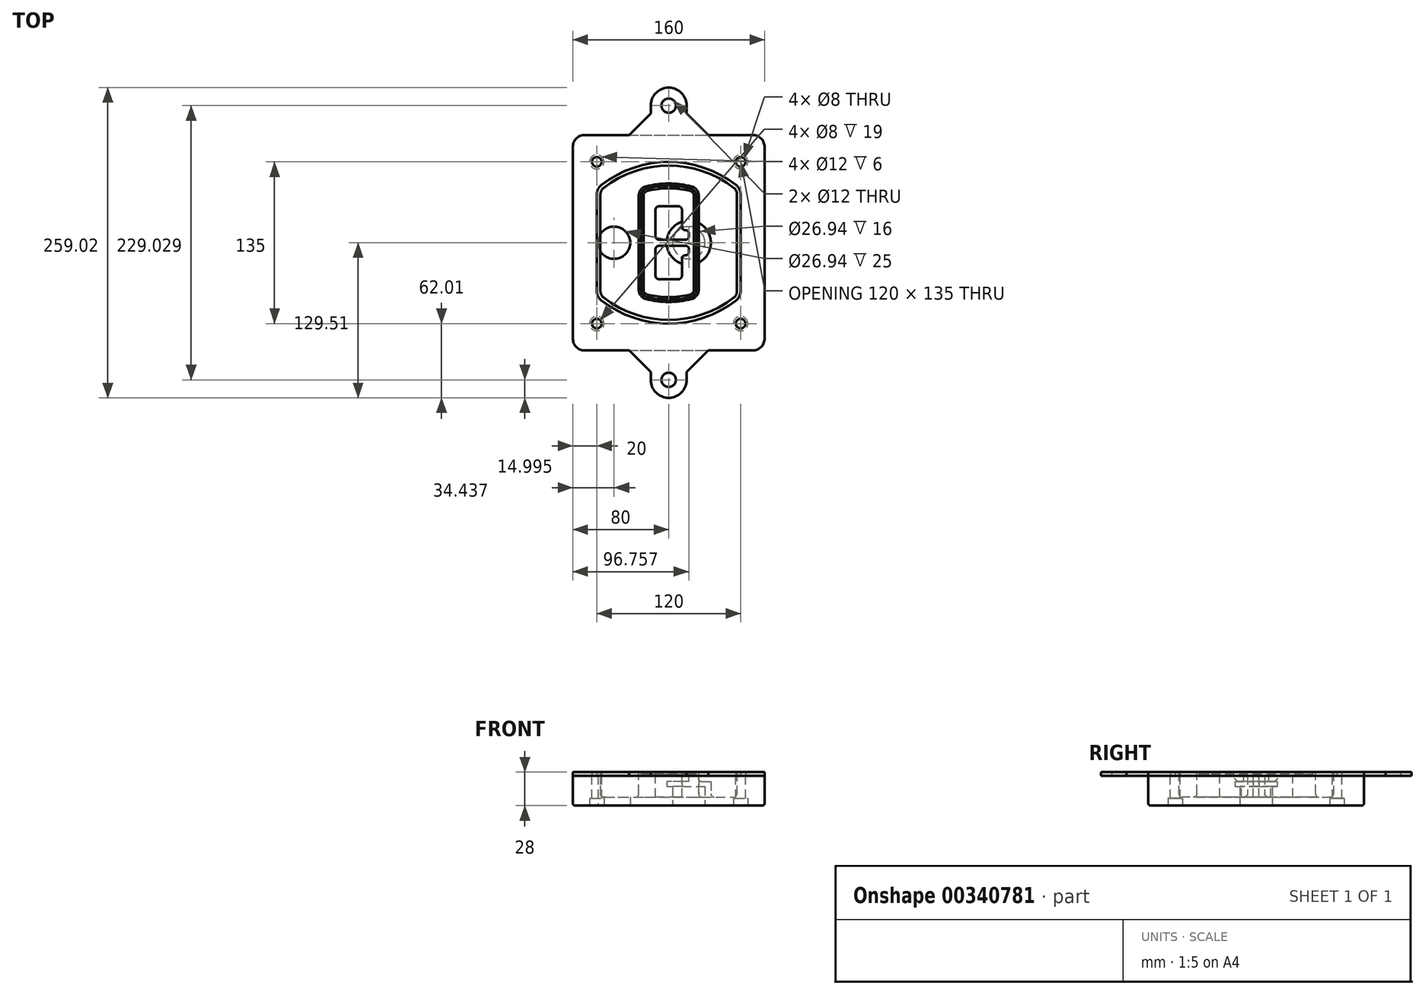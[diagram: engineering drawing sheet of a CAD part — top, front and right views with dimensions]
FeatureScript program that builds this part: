
annotation { "Feature Type Name" : "Feature", "Feature Type Description" : "" }
export const myFeature = defineFeature(function(context is Context, id is Id, definition is map)
    precondition{}
    {
        {
            var Q0;
            Q0=qCreatedBy(makeId("Top.planeOp"),FACE);
            var sketch = newSketch(context, id + "F0", { "sketchPlane" : qUnion([Q0])});
            skPoint(sketch, "E0.rect.middle", {"position": v(0, 0) * mm});
            skLineSegment(sketch, "E1.bottom", {"start": v(-70, -90) * mm, "end": v(70, -90) * mm});
            skLineSegment(sketch, "E1.top", {"start": v(-70, 90) * mm, "end": v(70, 90) * mm});
            skLineSegment(sketch, "E1.left", {"start": v(-80, -80) * mm, "end": v(-80, 80) * mm});
            skLineSegment(sketch, "E1.right", {"start": v(80, -80) * mm, "end": v(80, 80) * mm});
            skLineSegment(sketch, "E2", {"start": v(-80, 90) * mm, "end": v(80, -90) * mm, "construction": true});
            skLineSegment(sketch, "E3", {"start": v(80, 90) * mm, "end": v(-80, -90) * mm, "construction": true});
            skCircle(sketch, "E4", {"center": v(-60, 67.5) * mm, "radius": 4 * mm});
            skCircle(sketch, "E5", {"center": v(60, 67.5) * mm, "radius": 4 * mm});
            skCircle(sketch, "E6", {"center": v(60, -67.5) * mm, "radius": 4 * mm});
            skCircle(sketch, "E7", {"center": v(-60, -67.5) * mm, "radius": 4 * mm});
            skLineSegment(sketch, "E8", {"start": v(-60, 67.5) * mm, "end": v(60, 67.5) * mm, "construction": true});
            skLineSegment(sketch, "E9", {"start": v(60, 67.5) * mm, "end": v(60, -67.5) * mm, "construction": true});
            skLineSegment(sketch, "E10", {"start": v(60, -67.5) * mm, "end": v(-60, -67.5) * mm, "construction": true});
            skLineSegment(sketch, "E11", {"start": v(-60, -67.5) * mm, "end": v(-60, 67.5) * mm, "construction": true});
            skLineSegment(sketch, "E12", {"start": v(-60, 40.3) * mm, "end": v(-60, -40.3) * mm});
            skLineSegment(sketch, "E13", {"start": v(60, 40.3) * mm, "end": v(60, -40.3) * mm});
            skArc(sketch, "E14", {"start": v(56.15, 48.18) * mm, "mid": v(0, 67.5) * mm, "end": v(-56.15, 48.18) * mm});
            skArc(sketch, "E15", {"start": v(-56.15, -48.18) * mm, "mid": v(0, -67.5) * mm, "end": v(56.15, -48.18) * mm});
            skLineSegment(sketch, "E16", {"start": v(-60, 0) * mm, "end": v(60, 0) * mm, "construction": true});
            skPoint(sketch, "E17.visualSharp", {"position": v(-60, -45) * mm});
            skArc(sketch, "E17.filletArc", {"start": v(-60, -40.3) * mm, "mid": v(-58.99, -44.68) * mm, "end": v(-56.15, -48.18) * mm});
            skPoint(sketch, "E18.visualSharp", {"position": v(-60, 45) * mm});
            skArc(sketch, "E18.filletArc", {"start": v(-56.15, 48.18) * mm, "mid": v(-58.99, 44.68) * mm, "end": v(-60, 40.3) * mm});
            skPoint(sketch, "E19.visualSharp", {"position": v(60, 45) * mm});
            skArc(sketch, "E19.filletArc", {"start": v(60, 40.3) * mm, "mid": v(58.99, 44.68) * mm, "end": v(56.15, 48.18) * mm});
            skPoint(sketch, "E20.visualSharp", {"position": v(60, -45) * mm});
            skArc(sketch, "E20.filletArc", {"start": v(56.15, -48.18) * mm, "mid": v(58.99, -44.68) * mm, "end": v(60, -40.3) * mm});
            skPoint(sketch, "E21.visualSharp", {"position": v(-80, 90) * mm});
            skArc(sketch, "E21.filletArc", {"start": v(-70, 90) * mm, "mid": v(-77.07, 87.07) * mm, "end": v(-80, 80) * mm});
            skPoint(sketch, "E22.visualSharp", {"position": v(80, 90) * mm});
            skArc(sketch, "E22.filletArc", {"start": v(80, 80) * mm, "mid": v(77.07, 87.07) * mm, "end": v(70, 90) * mm});
            skPoint(sketch, "E23.visualSharp", {"position": v(80, -90) * mm});
            skArc(sketch, "E23.filletArc", {"start": v(70, -90) * mm, "mid": v(77.07, -87.07) * mm, "end": v(80, -80) * mm});
            skPoint(sketch, "E24.visualSharp", {"position": v(-80, -90) * mm});
            skArc(sketch, "E24.filletArc", {"start": v(-80, -80) * mm, "mid": v(-77.07, -87.07) * mm, "end": v(-70, -90) * mm});
            skArc(sketch, "E25.0", {"start": v(57, 40.3) * mm, "mid": v(56.3, 43.36) * mm, "end": v(54.3, 45.81) * mm});
            skLineSegment(sketch, "E25.1", {"start": v(57, 40.3) * mm, "end": v(57, -40.3) * mm});
            skArc(sketch, "E25.2", {"start": v(54.3, -45.81) * mm, "mid": v(56.3, -43.36) * mm, "end": v(57, -40.3) * mm});
            skArc(sketch, "E25.3", {"start": v(-54.3, -45.81) * mm, "mid": v(0, -64.5) * mm, "end": v(54.3, -45.81) * mm});
            skArc(sketch, "E25.4", {"start": v(-57, -40.3) * mm, "mid": v(-56.3, -43.36) * mm, "end": v(-54.3, -45.81) * mm});
            skArc(sketch, "E25.5", {"start": v(54.3, 45.81) * mm, "mid": v(0, 64.5) * mm, "end": v(-54.3, 45.81) * mm});
            skLineSegment(sketch, "E25.6", {"start": v(-57, 40.3) * mm, "end": v(-57, -40.3) * mm});
            skArc(sketch, "E25.7", {"start": v(-54.3, 45.81) * mm, "mid": v(-56.3, 43.36) * mm, "end": v(-57, 40.3) * mm});
            skArc(sketch, "E26.0", {"start": v(-58.62, 51.33) * mm, "mid": v(-62.58, 46.43) * mm, "end": v(-64, 40.3) * mm});
            skArc(sketch, "E26.1", {"start": v(58.62, 51.33) * mm, "mid": v(0, 71.5) * mm, "end": v(-58.62, 51.33) * mm});
            skArc(sketch, "E26.2", {"start": v(64, 40.3) * mm, "mid": v(62.58, 46.43) * mm, "end": v(58.62, 51.33) * mm});
            skLineSegment(sketch, "E26.3", {"start": v(64, 40.3) * mm, "end": v(64, -40.3) * mm});
            skArc(sketch, "E26.4", {"start": v(58.62, -51.33) * mm, "mid": v(62.58, -46.43) * mm, "end": v(64, -40.3) * mm});
            skLineSegment(sketch, "E26.5", {"start": v(-64, 40.3) * mm, "end": v(-64, -40.3) * mm});
            skArc(sketch, "E26.6", {"start": v(-58.62, -51.33) * mm, "mid": v(0, -71.5) * mm, "end": v(58.62, -51.33) * mm});
            skArc(sketch, "E26.7", {"start": v(-64, -40.3) * mm, "mid": v(-62.58, -46.43) * mm, "end": v(-58.62, -51.33) * mm});
            skSolve(sketch);
        }
        {
            var Q0;
            Q0=makeQuery(id+"F0.imprint","IMPRINT",FACE,{"disambiguationData":[TD([[makeQuery(id+"F0.imprint","IMPRINT",EDGE,{"derivedFrom":sQuery(id+"F0.wireOp",EDGE,"E1.bottom")}),1.0]])]});
            var Q1;
            Q1=makeQuery(id+"F0.imprint","IMPRINT",FACE,{"disambiguationData":[TD([[makeQuery(id+"F0.imprint","IMPRINT",EDGE,{"derivedFrom":sQuery(id+"F0.wireOp",EDGE,"E12")}),1.0]])]});
            var Q2;
            Q2=makeQuery(id+"F0.imprint","IMPRINT",FACE,{"disambiguationData":[TD([[makeQuery(id+"F0.imprint","IMPRINT",EDGE,{"derivedFrom":sQuery(id+"F0.wireOp",EDGE,"E25.0")}),1.0]])]});
            var Q3;
            Q3=makeQuery(id+"F0.imprint","IMPRINT",FACE,{"disambiguationData":[TD([[makeQuery(id+"F0.imprint","IMPRINT",EDGE,{"derivedFrom":sQuery(id+"F0.wireOp",EDGE,"E12")}),-1.0]])]});
            extrude(context, id + "F1", {"entities" : qUnion([Q0, Q1, Q2, Q3]), "oppositeDirection" : true, "depth" : 25 * mm});
        }
        {
            var Q0;
            Q0=makeQuery(id+"F0.imprint","IMPRINT",FACE,{"disambiguationData":[TD([[makeQuery(id+"F0.imprint","IMPRINT",EDGE,{"derivedFrom":sQuery(id+"F0.wireOp",EDGE,"E12")}),1.0]])]});
            extrude(context, id + "F2", {"entities" : qUnion([Q0]), "operationType" : NewBodyOperationType.ADD, "depth" : 3 * mm});
        }
        {
            var Q0;
            Q0=makeQuery(id+"F0.imprint","IMPRINT",FACE,{"disambiguationData":[TD([[makeQuery(id+"F0.imprint","IMPRINT",EDGE,{"derivedFrom":sQuery(id+"F0.wireOp",EDGE,"E25.0")}),1.0]])]});
            extrude(context, id + "F3", {"entities" : qUnion([Q0]), "operationType" : NewBodyOperationType.REMOVE, "oppositeDirection" : true, "depth" : 18 * mm});
        }
        {
            var Q0;
            Q0=makeQuery(id+"F2.opExtrude","CAP_FACE",FACE,{"disambiguationData":[OSD([sQuery(id+"F0.wireOp",EDGE,"E12"),sQuery(id+"F0.wireOp",EDGE,"E13"),sQuery(id+"F0.wireOp",EDGE,"E14"),sQuery(id+"F0.wireOp",EDGE,"E15"),sQuery(id+"F0.wireOp",EDGE,"E17.filletArc"),sQuery(id+"F0.wireOp",EDGE,"E18.filletArc"),sQuery(id+"F0.wireOp",EDGE,"E19.filletArc"),sQuery(id+"F0.wireOp",EDGE,"E20.filletArc"),sQuery(id+"F0.wireOp",EDGE,"E25.0"),sQuery(id+"F0.wireOp",EDGE,"E25.1"),sQuery(id+"F0.wireOp",EDGE,"E25.2"),sQuery(id+"F0.wireOp",EDGE,"E25.3"),sQuery(id+"F0.wireOp",EDGE,"E25.4"),sQuery(id+"F0.wireOp",EDGE,"E25.5"),sQuery(id+"F0.wireOp",EDGE,"E25.6"),sQuery(id+"F0.wireOp",EDGE,"E25.7")])],"isStart":false});
            var sketch = newSketch(context, id + "F4", { "sketchPlane" : qUnion([Q0])});
            skArc(sketch, "E27.0", {"start": v(-19.08, -46.97) * mm, "mid": v(0, -49.5) * mm, "end": v(19.08, -46.97) * mm});
            skArc(sketch, "E28.0", {"start": v(19.08, 46.97) * mm, "mid": v(0, 49.5) * mm, "end": v(-19.08, 46.97) * mm});
            skLineSegment(sketch, "E29", {"start": v(-25, 39.25) * mm, "end": v(-25, -39.25) * mm});
            skLineSegment(sketch, "E30", {"start": v(25, 39.25) * mm, "end": v(25, -39.25) * mm});
            skLineSegment(sketch, "E31", {"start": v(-25, 45.1) * mm, "end": v(25, 45.1) * mm, "construction": true});
            skLineSegment(sketch, "E32", {"start": v(-25, -45.1) * mm, "end": v(25, -45.1) * mm, "construction": true});
            skPoint(sketch, "E33.visualSharp", {"position": v(-25, 45.1) * mm});
            skArc(sketch, "E33.filletArc", {"start": v(-19.08, 46.97) * mm, "mid": v(-23.35, 44.11) * mm, "end": v(-25, 39.25) * mm});
            skPoint(sketch, "E34.visualSharp", {"position": v(25, 45.1) * mm});
            skArc(sketch, "E34.filletArc", {"start": v(25, 39.25) * mm, "mid": v(23.35, 44.11) * mm, "end": v(19.08, 46.97) * mm});
            skPoint(sketch, "E35.visualSharp", {"position": v(25, -45.1) * mm});
            skArc(sketch, "E35.filletArc", {"start": v(19.08, -46.97) * mm, "mid": v(23.35, -44.11) * mm, "end": v(25, -39.25) * mm});
            skPoint(sketch, "E36.visualSharp", {"position": v(-25, -45.1) * mm});
            skArc(sketch, "E36.filletArc", {"start": v(-25, -39.25) * mm, "mid": v(-23.35, -44.11) * mm, "end": v(-19.08, -46.97) * mm});
            skArc(sketch, "E37.0", {"start": v(54.3, 45.81) * mm, "mid": v(0, 64.5) * mm, "end": v(-54.3, 45.81) * mm});
            skArc(sketch, "E37.1", {"start": v(-54.3, 45.81) * mm, "mid": v(-56.3, 43.36) * mm, "end": v(-57, 40.3) * mm});
            skLineSegment(sketch, "E37.2", {"start": v(-57, 40.3) * mm, "end": v(-57, -40.3) * mm});
            skArc(sketch, "E37.3", {"start": v(-57, -40.3) * mm, "mid": v(-56.3, -43.36) * mm, "end": v(-54.3, -45.81) * mm});
            skArc(sketch, "E37.4", {"start": v(-54.3, -45.81) * mm, "mid": v(0, -64.5) * mm, "end": v(54.3, -45.81) * mm});
            skArc(sketch, "E37.5", {"start": v(54.3, -45.81) * mm, "mid": v(56.3, -43.36) * mm, "end": v(57, -40.3) * mm});
            skLineSegment(sketch, "E37.6", {"start": v(57, 40.3) * mm, "end": v(57, -40.3) * mm});
            skArc(sketch, "E37.7", {"start": v(57, 40.3) * mm, "mid": v(56.3, 43.36) * mm, "end": v(54.3, 45.81) * mm});
            skLineSegment(sketch, "E38.0", {"start": v(23, 39.25) * mm, "end": v(23, -39.25) * mm});
            skArc(sketch, "E38.1", {"start": v(18.56, -45.04) * mm, "mid": v(21.76, -42.9) * mm, "end": v(23, -39.25) * mm});
            skArc(sketch, "E38.2", {"start": v(-18.56, -45.04) * mm, "mid": v(0, -47.5) * mm, "end": v(18.56, -45.04) * mm});
            skArc(sketch, "E38.3", {"start": v(-23, -39.25) * mm, "mid": v(-21.76, -42.9) * mm, "end": v(-18.56, -45.04) * mm});
            skLineSegment(sketch, "E38.4", {"start": v(-23, 39.25) * mm, "end": v(-23, -39.25) * mm});
            skArc(sketch, "E38.5", {"start": v(23, 39.25) * mm, "mid": v(21.76, 42.9) * mm, "end": v(18.56, 45.04) * mm});
            skArc(sketch, "E38.6", {"start": v(-18.56, 45.04) * mm, "mid": v(-21.76, 42.9) * mm, "end": v(-23, 39.25) * mm});
            skArc(sketch, "E38.7", {"start": v(18.56, 45.04) * mm, "mid": v(0, 47.5) * mm, "end": v(-18.56, 45.04) * mm});
            skArc(sketch, "E39.0", {"start": v(21, 39.25) * mm, "mid": v(20.18, 41.68) * mm, "end": v(18.04, 43.1) * mm});
            skLineSegment(sketch, "E39.1", {"start": v(21, 39.25) * mm, "end": v(21, -39.25) * mm});
            skArc(sketch, "E39.2", {"start": v(18.04, -43.1) * mm, "mid": v(20.18, -41.68) * mm, "end": v(21, -39.25) * mm});
            skArc(sketch, "E39.3", {"start": v(-18.04, -43.1) * mm, "mid": v(0, -45.5) * mm, "end": v(18.04, -43.1) * mm});
            skArc(sketch, "E39.4", {"start": v(-21, -39.25) * mm, "mid": v(-20.18, -41.68) * mm, "end": v(-18.04, -43.1) * mm});
            skArc(sketch, "E39.5", {"start": v(18.04, 43.1) * mm, "mid": v(0, 45.5) * mm, "end": v(-18.04, 43.1) * mm});
            skLineSegment(sketch, "E39.6", {"start": v(-21, 39.25) * mm, "end": v(-21, -39.25) * mm});
            skArc(sketch, "E39.7", {"start": v(-18.04, 43.1) * mm, "mid": v(-20.18, 41.68) * mm, "end": v(-21, 39.25) * mm});
            skLineSegment(sketch, "E40", {"start": v(-25, 0) * mm, "end": v(25, 0) * mm, "construction": true});
            skLineSegment(sketch, "E41", {"start": v(-11, 5.5) * mm, "end": v(-11, 27.5) * mm});
            skLineSegment(sketch, "E42", {"start": v(-8, 30.5) * mm, "end": v(8, 30.5) * mm});
            skLineSegment(sketch, "E43", {"start": v(11, 27.5) * mm, "end": v(11, 13.5) * mm});
            skLineSegment(sketch, "E44", {"start": v(14, 10.5) * mm, "end": v(14, 10.5) * mm});
            skLineSegment(sketch, "E45", {"start": v(17, 7.5) * mm, "end": v(17, 5.5) * mm});
            skLineSegment(sketch, "E46", {"start": v(14, 2.5) * mm, "end": v(-8, 2.5) * mm});
            skPoint(sketch, "E47.visualSharp", {"position": v(-11, 30.5) * mm});
            skArc(sketch, "E47.filletArc", {"start": v(-8, 30.5) * mm, "mid": v(-10.12, 29.62) * mm, "end": v(-11, 27.5) * mm});
            skPoint(sketch, "E48.visualSharp", {"position": v(11, 30.5) * mm});
            skArc(sketch, "E48.filletArc", {"start": v(11, 27.5) * mm, "mid": v(10.12, 29.62) * mm, "end": v(8, 30.5) * mm});
            skPoint(sketch, "E49.visualSharp", {"position": v(11, 10.5) * mm});
            skArc(sketch, "E49.filletArc", {"start": v(11, 13.5) * mm, "mid": v(11.88, 11.38) * mm, "end": v(14, 10.5) * mm});
            skPoint(sketch, "E50.visualSharp", {"position": v(17, 10.5) * mm});
            skArc(sketch, "E50.filletArc", {"start": v(17, 7.5) * mm, "mid": v(16.12, 9.62) * mm, "end": v(14, 10.5) * mm});
            skPoint(sketch, "E51.visualSharp", {"position": v(17, 2.5) * mm});
            skArc(sketch, "E51.filletArc", {"start": v(14, 2.5) * mm, "mid": v(16.12, 3.38) * mm, "end": v(17, 5.5) * mm});
            skPoint(sketch, "E52.visualSharp", {"position": v(-11, 2.5) * mm});
            skArc(sketch, "E52.filletArc", {"start": v(-11, 5.5) * mm, "mid": v(-10.12, 3.38) * mm, "end": v(-8, 2.5) * mm});
            skLineSegment(sketch, "E53.0.MirrorCS", {"start": v(14, -2.5) * mm, "end": v(-8, -2.5) * mm});
            skArc(sketch, "E54.0.MirrorCS", {"start": v(-11, -5.5) * mm, "mid": v(-10.12, -3.38) * mm, "end": v(-8, -2.5) * mm});
            skLineSegment(sketch, "E55.0.MirrorCS", {"start": v(-11, -5.5) * mm, "end": v(-11, -27.5) * mm});
            skArc(sketch, "E56.0.MirrorCS", {"start": v(-8, -30.5) * mm, "mid": v(-10.12, -29.62) * mm, "end": v(-11, -27.5) * mm});
            skLineSegment(sketch, "E57.0.MirrorCS", {"start": v(-8, -30.5) * mm, "end": v(8, -30.5) * mm});
            skArc(sketch, "E58.0.MirrorCS", {"start": v(11, -27.5) * mm, "mid": v(10.12, -29.62) * mm, "end": v(8, -30.5) * mm});
            skLineSegment(sketch, "E59.0.MirrorCS", {"start": v(11, -27.5) * mm, "end": v(11, -13.5) * mm});
            skArc(sketch, "E60.0.MirrorCS", {"start": v(11, -13.5) * mm, "mid": v(11.88, -11.38) * mm, "end": v(14, -10.5) * mm});
            skArc(sketch, "E61.0.MirrorCS", {"start": v(17, -7.5) * mm, "mid": v(16.12, -9.62) * mm, "end": v(14, -10.5) * mm});
            skLineSegment(sketch, "E62.0.MirrorCS", {"start": v(17, -7.5) * mm, "end": v(17, -5.5) * mm});
            skArc(sketch, "E63.0.MirrorCS", {"start": v(14, -2.5) * mm, "mid": v(16.12, -3.38) * mm, "end": v(17, -5.5) * mm});
            skSolve(sketch);
        }
        {
            var Q0;
            Q0=makeQuery(id+"F4.imprint","IMPRINT",FACE,{"disambiguationData":[TD([[makeQuery(id+"F4.imprint","IMPRINT",EDGE,{"derivedFrom":sQuery(id+"F4.wireOp",EDGE,"E27.0")}),1.0]])]});
            var Q1;
            Q1=makeQuery(id+"F4.imprint","IMPRINT",FACE,{"disambiguationData":[TD([[makeQuery(id+"F4.imprint","IMPRINT",EDGE,{"derivedFrom":sQuery(id+"F4.wireOp",EDGE,"E38.0")}),-1.0]])]});
            var Q2;
            Q2=makeQuery(id+"F4.imprint","IMPRINT",FACE,{"disambiguationData":[TD([[makeQuery(id+"F4.imprint","IMPRINT",EDGE,{"derivedFrom":sQuery(id+"F4.wireOp",EDGE,"E39.0")}),1.0]])]});
            extrude(context, id + "F5", {"entities" : qUnion([Q0, Q1, Q2]), "operationType" : NewBodyOperationType.ADD, "endBound" : BoundingType.UP_TO_NEXT, "oppositeDirection" : true, "depth" : 25 * mm});
        }
        {
            var Q0;
            Q0=makeQuery(id+"F4.imprint","IMPRINT",FACE,{"disambiguationData":[TD([[makeQuery(id+"F4.imprint","IMPRINT",EDGE,{"derivedFrom":sQuery(id+"F4.wireOp",EDGE,"E38.0")}),-1.0]])]});
            extrude(context, id + "F6", {"entities" : qUnion([Q0]), "operationType" : NewBodyOperationType.REMOVE, "oppositeDirection" : true, "depth" : 2 * mm});
        }
        {
            var Q0;
            Q0=makeQuery(id+"F1.opExtrude","CAP_FACE",FACE,{"disambiguationData":[OSD([sQuery(id+"F0.wireOp",EDGE,"E1.bottom"),sQuery(id+"F0.wireOp",EDGE,"E1.top"),sQuery(id+"F0.wireOp",EDGE,"E1.left"),sQuery(id+"F0.wireOp",EDGE,"E1.right"),sQuery(id+"F0.wireOp",EDGE,"E4"),sQuery(id+"F0.wireOp",EDGE,"E5"),sQuery(id+"F0.wireOp",EDGE,"E6"),sQuery(id+"F0.wireOp",EDGE,"E7"),sQuery(id+"F0.wireOp",EDGE,"E21.filletArc"),sQuery(id+"F0.wireOp",EDGE,"E22.filletArc"),sQuery(id+"F0.wireOp",EDGE,"E23.filletArc"),sQuery(id+"F0.wireOp",EDGE,"E24.filletArc")])],"isStart":false});
            var sketch = newSketch(context, id + "F7", { "sketchPlane" : qUnion([Q0])});
            skCircle(sketch, "E64", {"center": v(16.76, 0) * mm, "radius": 13.47 * mm});
            skCircle(sketch, "E65", {"center": v(-45.56, 0) * mm, "radius": 13.47 * mm});
            skLineSegment(sketch, "E66", {"start": v(80, 0) * mm, "end": v(-80, 0) * mm});
            skCircle(sketch, "E67", {"center": v(16.76, 0) * mm, "radius": 18.47 * mm});
            skCircle(sketch, "E68", {"center": v(60, -67.5) * mm, "radius": 6 * mm});
            skCircle(sketch, "E69", {"center": v(-60, -67.5) * mm, "radius": 6 * mm});
            skCircle(sketch, "E70", {"center": v(-60, 67.5) * mm, "radius": 6 * mm});
            skCircle(sketch, "E71", {"center": v(60, 67.5) * mm, "radius": 6 * mm});
            skSolve(sketch);
        }
        {
            var Q0;
            {var subQ1=sQuery(id+"F7.wireOp",EDGE,"E66");var subQ4=sQuery(id+"F7.wireOp",EDGE,"E64");var subQ6=makeQuery(id+"F7.imprint","INTERSECT",VERTEX,{"disambiguationData":[OD(0.0)],"derivedFrom":[subQ4,subQ1]});Q0=makeQuery(id+"F7.imprint","IMPRINT",FACE,{"disambiguationData":[TD([[makeQuery(id+"F7.imprint","IMPRINT",EDGE,{"disambiguationData":[TD([[subQ6,-1.0]])],"derivedFrom":subQ4}),-1.0]])]});}
            var Q1;
            {var subQ0=sQuery(id+"F7.wireOp",EDGE,"E66");var subQ1=sQuery(id+"F7.wireOp",EDGE,"E64");var subQ3=makeQuery(id+"F7.imprint","INTERSECT",VERTEX,{"disambiguationData":[OD(0.0)],"derivedFrom":[subQ1,subQ0]});Q1=makeQuery(id+"F7.imprint","IMPRINT",FACE,{"disambiguationData":[TD([[makeQuery(id+"F7.imprint","IMPRINT",EDGE,{"disambiguationData":[TD([[subQ3,-1.0]])],"derivedFrom":subQ1}),1.0]])]});}
            var Q2;
            {var subQ0=sQuery(id+"F7.wireOp",EDGE,"E66");var subQ1=sQuery(id+"F7.wireOp",EDGE,"E64");var subQ3=makeQuery(id+"F7.imprint","INTERSECT",VERTEX,{"disambiguationData":[OD(0.0)],"derivedFrom":[subQ1,subQ0]});Q2=makeQuery(id+"F7.imprint","IMPRINT",FACE,{"disambiguationData":[TD([[makeQuery(id+"F7.imprint","IMPRINT",EDGE,{"disambiguationData":[TD([[subQ3,1.0]])],"derivedFrom":subQ1}),1.0]])]});}
            var Q3;
            {var subQ1=sQuery(id+"F7.wireOp",EDGE,"E66");var subQ4=sQuery(id+"F7.wireOp",EDGE,"E64");var subQ6=makeQuery(id+"F7.imprint","INTERSECT",VERTEX,{"disambiguationData":[OD(0.0)],"derivedFrom":[subQ4,subQ1]});Q3=makeQuery(id+"F7.imprint","IMPRINT",FACE,{"disambiguationData":[TD([[makeQuery(id+"F7.imprint","IMPRINT",EDGE,{"disambiguationData":[TD([[subQ6,1.0]])],"derivedFrom":subQ4}),-1.0]])]});}
            extrude(context, id + "F8", {"entities" : qUnion([Q0, Q1, Q2, Q3]), "operationType" : NewBodyOperationType.ADD, "oppositeDirection" : true, "depth" : 20 * mm});
        }
        {
            var Q0;
            {var subQ0=sQuery(id+"F7.wireOp",EDGE,"E66");var subQ1=sQuery(id+"F7.wireOp",EDGE,"E64");var subQ3=makeQuery(id+"F7.imprint","INTERSECT",VERTEX,{"disambiguationData":[OD(0.0)],"derivedFrom":[subQ1,subQ0]});Q0=makeQuery(id+"F7.imprint","IMPRINT",FACE,{"disambiguationData":[TD([[makeQuery(id+"F7.imprint","IMPRINT",EDGE,{"disambiguationData":[TD([[subQ3,-1.0]])],"derivedFrom":subQ1}),1.0]])]});}
            var Q1;
            {var subQ0=sQuery(id+"F7.wireOp",EDGE,"E66");var subQ1=sQuery(id+"F7.wireOp",EDGE,"E64");var subQ3=makeQuery(id+"F7.imprint","INTERSECT",VERTEX,{"disambiguationData":[OD(0.0)],"derivedFrom":[subQ1,subQ0]});Q1=makeQuery(id+"F7.imprint","IMPRINT",FACE,{"disambiguationData":[TD([[makeQuery(id+"F7.imprint","IMPRINT",EDGE,{"disambiguationData":[TD([[subQ3,1.0]])],"derivedFrom":subQ1}),1.0]])]});}
            extrude(context, id + "F9", {"entities" : qUnion([Q0, Q1]), "operationType" : NewBodyOperationType.REMOVE, "oppositeDirection" : true, "depth" : 16 * mm});
        }
        {
            var Q0;
            {var subQ0=sQuery(id+"F7.wireOp",EDGE,"E66");var subQ1=sQuery(id+"F7.wireOp",EDGE,"E65");var subQ3=makeQuery(id+"F7.imprint","INTERSECT",VERTEX,{"disambiguationData":[OD(0.0)],"derivedFrom":[subQ1,subQ0]});Q0=makeQuery(id+"F7.imprint","IMPRINT",FACE,{"disambiguationData":[TD([[makeQuery(id+"F7.imprint","IMPRINT",EDGE,{"disambiguationData":[TD([[subQ3,-1.0]])],"derivedFrom":subQ1}),1.0]])]});}
            var Q1;
            {var subQ0=sQuery(id+"F7.wireOp",EDGE,"E66");var subQ1=sQuery(id+"F7.wireOp",EDGE,"E65");var subQ3=makeQuery(id+"F7.imprint","INTERSECT",VERTEX,{"disambiguationData":[OD(0.0)],"derivedFrom":[subQ1,subQ0]});Q1=makeQuery(id+"F7.imprint","IMPRINT",FACE,{"disambiguationData":[TD([[makeQuery(id+"F7.imprint","IMPRINT",EDGE,{"disambiguationData":[TD([[subQ3,1.0]])],"derivedFrom":subQ1}),1.0]])]});}
            extrude(context, id + "F10", {"entities" : qUnion([Q0, Q1]), "operationType" : NewBodyOperationType.REMOVE, "oppositeDirection" : true, "depth" : 25 * mm});
        }
        {
            var Q0;
            Q0=makeQuery(id+"F7.imprint","IMPRINT",FACE,{"disambiguationData":[TD([[makeQuery(id+"F7.imprint","IMPRINT",EDGE,{"derivedFrom":sQuery(id+"F7.wireOp",EDGE,"E68")}),1.0]])]});
            var Q1;
            Q1=makeQuery(id+"F7.imprint","IMPRINT",FACE,{"disambiguationData":[TD([[makeQuery(id+"F7.imprint","IMPRINT",EDGE,{"derivedFrom":makeQuery(id+"F1.opExtrude","CAP_EDGE",EDGE,{"disambiguationData":[OSD([sQuery(id+"F0.wireOp",EDGE,"E5")])],"isStart":false})}),-1.0]])]});
            var Q2;
            Q2=makeQuery(id+"F7.imprint","IMPRINT",FACE,{"disambiguationData":[TD([[makeQuery(id+"F7.imprint","IMPRINT",EDGE,{"derivedFrom":sQuery(id+"F7.wireOp",EDGE,"E69")}),1.0]])]});
            var Q3;
            Q3=makeQuery(id+"F7.imprint","IMPRINT",FACE,{"disambiguationData":[TD([[makeQuery(id+"F7.imprint","IMPRINT",EDGE,{"derivedFrom":makeQuery(id+"F1.opExtrude","CAP_EDGE",EDGE,{"disambiguationData":[OSD([sQuery(id+"F0.wireOp",EDGE,"E4")])],"isStart":false})}),-1.0]])]});
            var Q4;
            Q4=makeQuery(id+"F7.imprint","IMPRINT",FACE,{"disambiguationData":[TD([[makeQuery(id+"F7.imprint","IMPRINT",EDGE,{"derivedFrom":sQuery(id+"F7.wireOp",EDGE,"E70")}),1.0]])]});
            var Q5;
            Q5=makeQuery(id+"F7.imprint","IMPRINT",FACE,{"disambiguationData":[TD([[makeQuery(id+"F7.imprint","IMPRINT",EDGE,{"derivedFrom":makeQuery(id+"F1.opExtrude","CAP_EDGE",EDGE,{"disambiguationData":[OSD([sQuery(id+"F0.wireOp",EDGE,"E7")])],"isStart":false})}),-1.0]])]});
            var Q6;
            Q6=makeQuery(id+"F7.imprint","IMPRINT",FACE,{"disambiguationData":[TD([[makeQuery(id+"F7.imprint","IMPRINT",EDGE,{"derivedFrom":sQuery(id+"F7.wireOp",EDGE,"E71")}),1.0]])]});
            var Q7;
            Q7=makeQuery(id+"F7.imprint","IMPRINT",FACE,{"disambiguationData":[TD([[makeQuery(id+"F7.imprint","IMPRINT",EDGE,{"derivedFrom":makeQuery(id+"F1.opExtrude","CAP_EDGE",EDGE,{"disambiguationData":[OSD([sQuery(id+"F0.wireOp",EDGE,"E6")])],"isStart":false})}),-1.0]])]});
            extrude(context, id + "F11", {"entities" : qUnion([Q0, Q1, Q2, Q3, Q4, Q5, Q6, Q7]), "operationType" : NewBodyOperationType.REMOVE, "oppositeDirection" : true, "depth" : 6 * mm});
        }
        {
            var Q0;
            Q0=makeQuery(id+"F9.boolean.opBoolean","COPY",FACE,{"derivedFrom":makeQuery(id+"F9.opExtrude","CAP_FACE",FACE,{"disambiguationData":[OSD([sQuery(id+"F7.wireOp",EDGE,"E64")])],"isStart":false})});
            var sketch = newSketch(context, id + "F12", { "sketchPlane" : qUnion([Q0])});
            skArc(sketch, "E72.0", {"start": v(11, 17.55) * mm, "mid": v(2.57, 11.82) * mm, "end": v(-1.54, 2.5) * mm});
            skArc(sketch, "E72.1", {"start": v(-1.54, -2.5) * mm, "mid": v(2.57, -11.82) * mm, "end": v(11, -17.55) * mm});
            skLineSegment(sketch, "E73", {"start": v(-1.54, -2.5) * mm, "end": v(14, -2.5) * mm});
            skLineSegment(sketch, "E74.0", {"start": v(14, 2.5) * mm, "end": v(-1.54, 2.5) * mm});
            skArc(sketch, "E74.1", {"start": v(14, 2.5) * mm, "mid": v(16.12, 3.38) * mm, "end": v(17, 5.5) * mm});
            skLineSegment(sketch, "E74.2", {"start": v(17, 7.5) * mm, "end": v(17, 5.5) * mm});
            skArc(sketch, "E74.3", {"start": v(17, 7.5) * mm, "mid": v(16.12, 9.62) * mm, "end": v(14, 10.5) * mm});
            skArc(sketch, "E74.4", {"start": v(11, 13.5) * mm, "mid": v(11.88, 11.38) * mm, "end": v(14, 10.5) * mm});
            skLineSegment(sketch, "E74.5", {"start": v(11, 17.55) * mm, "end": v(11, 13.5) * mm});
            skLineSegment(sketch, "E74.7", {"start": v(14, -2.5) * mm, "end": v(-1.54, -2.5) * mm});
            skArc(sketch, "E74.8", {"start": v(14, -2.5) * mm, "mid": v(16.12, -3.38) * mm, "end": v(17, -5.5) * mm});
            skLineSegment(sketch, "E74.9", {"start": v(17, -7.5) * mm, "end": v(17, -5.5) * mm});
            skArc(sketch, "E74.10", {"start": v(17, -7.5) * mm, "mid": v(16.12, -9.62) * mm, "end": v(14, -10.5) * mm});
            skArc(sketch, "E74.11", {"start": v(11, -13.5) * mm, "mid": v(11.88, -11.38) * mm, "end": v(14, -10.5) * mm});
            skLineSegment(sketch, "E74.12", {"start": v(11, -17.55) * mm, "end": v(11, -13.5) * mm});
            skPoint(sketch, "E75.orphan", {"position": v(11, -27.5) * mm});
            skPoint(sketch, "E76.orphan", {"position": v(-8, -2.5) * mm});
            skPoint(sketch, "E77.orphan", {"position": v(-8, 2.5) * mm});
            skPoint(sketch, "E78.orphan", {"position": v(11, 27.5) * mm});
            skSolve(sketch);
        }
        {
            var Q0;
            {var subQ7=sQuery(id+"F12.wireOp",EDGE,"E72.0");var subQ14=sQuery(id+"F12.wireOp",EDGE,"E72.1");var subQ16=sQuery(id+"F12.wireOp",EDGE,"E74.1");var subQ18=sQuery(id+"F12.wireOp",EDGE,"E74.8");Q0=qUnion([makeQuery(id+"F12.imprint","IMPRINT",FACE,{"disambiguationData":[TD([[makeQuery(id+"F12.imprint","IMPRINT",EDGE,{"derivedFrom":subQ7}),1.0]])]}),makeQuery(id+"F12.imprint","IMPRINT",FACE,{"disambiguationData":[TD([[makeQuery(id+"F12.imprint","IMPRINT",EDGE,{"derivedFrom":subQ14}),1.0]])]}),makeQuery(id+"F12.imprint","IMPRINT",FACE,{"disambiguationData":[TD([[makeQuery(id+"F12.imprint","IMPRINT",EDGE,{"derivedFrom":subQ16}),1.0]])]}),makeQuery(id+"F12.imprint","IMPRINT",FACE,{"disambiguationData":[TD([[makeQuery(id+"F12.imprint","IMPRINT",EDGE,{"derivedFrom":subQ18}),-1.0]])]})]);}
            var Q1;
            Q1=makeQuery(id+"F5.boolean.opBoolean","SPLIT",FACE,{"disambiguationData":[TD([makeQuery(id+"F5.opExtrude","SWEPT_FACE",FACE,{"disambiguationData":[OSD([sQuery(id+"F4.wireOp",EDGE,"E41")])]})])],"derivedFrom":makeQuery(id+"F3.boolean.opBoolean","COPY",FACE,{"derivedFrom":makeQuery(id+"F3.opExtrude","CAP_FACE",FACE,{"disambiguationData":[OSD([sQuery(id+"F0.wireOp",EDGE,"E25.0"),sQuery(id+"F0.wireOp",EDGE,"E25.1"),sQuery(id+"F0.wireOp",EDGE,"E25.2"),sQuery(id+"F0.wireOp",EDGE,"E25.3"),sQuery(id+"F0.wireOp",EDGE,"E25.4"),sQuery(id+"F0.wireOp",EDGE,"E25.5"),sQuery(id+"F0.wireOp",EDGE,"E25.6"),sQuery(id+"F0.wireOp",EDGE,"E25.7")])],"isStart":false})})});
            extrude(context, id + "F13", {"entities" : qUnion([Q0]), "operationType" : NewBodyOperationType.REMOVE, "endBound" : BoundingType.UP_TO_SURFACE, "endBoundEntityFace" : qUnion([Q1]), "depth" : 25 * mm});
        }
        {
            var Q0;
            Q0=makeQuery(id+"F3.boolean.opBoolean","COPY",EDGE,{"derivedFrom":makeQuery(id+"F3.opExtrude","CAP_EDGE",EDGE,{"disambiguationData":[OSD([sQuery(id+"F0.wireOp",EDGE,"E25.6")])],"isStart":false})});
            var Q1;
            Q1=makeQuery(id+"F8.boolean.opBoolean","INTERSECT",EDGE,{"derivedFrom":[makeQuery(id+"F5.opExtrude","SWEPT_FACE",FACE,{"disambiguationData":[OSD([sQuery(id+"F4.wireOp",EDGE,"E30")])]}),makeQuery(id+"F8.opExtrude","CAP_FACE",FACE,{"disambiguationData":[OSD([sQuery(id+"F7.wireOp",EDGE,"E67")])],"isStart":false})]});
            var Q2;
            Q2=makeQuery(id+"F8.boolean.opBoolean","INTERSECT",EDGE,{"disambiguationData":[OD(1.0)],"derivedFrom":[makeQuery(id+"F5.opExtrude","SWEPT_FACE",FACE,{"disambiguationData":[OSD([sQuery(id+"F4.wireOp",EDGE,"E30")])]}),makeQuery(id+"F8.opExtrude","SWEPT_FACE",FACE,{"disambiguationData":[OSD([sQuery(id+"F7.wireOp",EDGE,"E67")])]})]});
            var Q3;
            {var subQ0=sQuery(id+"F4.wireOp",EDGE,"E30");Q3=makeQuery(id+"F8.boolean.opBoolean","SPLIT",EDGE,{"disambiguationData":[TD([makeQuery(id+"F5.opExtrude","SWEPT_FACE",FACE,{"disambiguationData":[OSD([sQuery(id+"F4.wireOp",EDGE,"E35.filletArc")])]})])],"derivedFrom":makeQuery(id+"F5.opExtrude","CAP_EDGE",EDGE,{"disambiguationData":[OSD([subQ0])],"isStart":false})});}
            var Q4;
            {var subQ0=sQuery(id+"F0.wireOp",EDGE,"E25.7");var subQ1=sQuery(id+"F0.wireOp",EDGE,"E25.1");var subQ2=sQuery(id+"F0.wireOp",EDGE,"E25.6");var subQ3=sQuery(id+"F0.wireOp",EDGE,"E25.5");var subQ4=sQuery(id+"F0.wireOp",EDGE,"E25.4");var subQ5=sQuery(id+"F0.wireOp",EDGE,"E25.0");var subQ6=sQuery(id+"F0.wireOp",EDGE,"E25.2");var subQ7=sQuery(id+"F0.wireOp",EDGE,"E25.3");Q4=makeQuery(id+"F8.boolean.opBoolean","INTERSECT",EDGE,{"derivedFrom":[makeQuery(id+"F5.boolean.opBoolean","SPLIT",FACE,{"disambiguationData":[TD([makeQuery(id+"F2.opExtrude","SWEPT_FACE",FACE,{"disambiguationData":[OSD([subQ5])]})])],"derivedFrom":makeQuery(id+"F3.boolean.opBoolean","COPY",FACE,{"derivedFrom":makeQuery(id+"F3.opExtrude","CAP_FACE",FACE,{"disambiguationData":[OSD([subQ5,subQ1,subQ6,subQ7,subQ4,subQ3,subQ2,subQ0])],"isStart":false})})}),makeQuery(id+"F8.opExtrude","SWEPT_FACE",FACE,{"disambiguationData":[OSD([sQuery(id+"F7.wireOp",EDGE,"E67")])]})]});}
            var Q5;
            Q5=makeQuery(id+"F8.boolean.opBoolean","INTERSECT",EDGE,{"disambiguationData":[OD(0.0)],"derivedFrom":[makeQuery(id+"F5.opExtrude","SWEPT_FACE",FACE,{"disambiguationData":[OSD([sQuery(id+"F4.wireOp",EDGE,"E30")])]}),makeQuery(id+"F8.opExtrude","SWEPT_FACE",FACE,{"disambiguationData":[OSD([sQuery(id+"F7.wireOp",EDGE,"E67")])]})]});
            fillet(context, id + "F14", {"entities" : qUnion([Q0, Q1, Q2, Q3, Q4, Q5]), "radius" : 3 * mm, "tangentPropagation" : true, "allowEdgeOverflow" : false});
        }
        {
            var Q0;
            Q0=makeQuery(id+"F1.opExtrude","CAP_EDGE",EDGE,{"disambiguationData":[OSD([sQuery(id+"F0.wireOp",EDGE,"E1.bottom")])],"isStart":false});
            fillet(context, id + "F15", {"entities" : qUnion([Q0]), "radius" : 2 * mm, "tangentPropagation" : true, "allowEdgeOverflow" : false});
        }
        {
            var Q0;
            {var subQ0=sQuery(id+"F0.wireOp",EDGE,"E21.filletArc");var subQ1=sQuery(id+"F0.wireOp",EDGE,"E7");var subQ2=sQuery(id+"F0.wireOp",EDGE,"E6");var subQ3=sQuery(id+"F0.wireOp",EDGE,"E5");var subQ4=sQuery(id+"F0.wireOp",EDGE,"E4");var subQ5=sQuery(id+"F0.wireOp",EDGE,"E22.filletArc");var subQ6=sQuery(id+"F0.wireOp",EDGE,"E1.bottom");var subQ7=sQuery(id+"F0.wireOp",EDGE,"E1.right");var subQ8=sQuery(id+"F0.wireOp",EDGE,"E1.top");var subQ9=sQuery(id+"F0.wireOp",EDGE,"E1.left");var subQ10=sQuery(id+"F0.wireOp",EDGE,"E23.filletArc");var subQ11=sQuery(id+"F0.wireOp",EDGE,"E24.filletArc");Q0=makeQuery(id+"F2.boolean.opBoolean","SPLIT",FACE,{"disambiguationData":[TD([makeQuery(id+"F1.opExtrude","SWEPT_FACE",FACE,{"disambiguationData":[OSD([subQ6])]})])],"derivedFrom":makeQuery(id+"F1.opExtrude","CAP_FACE",FACE,{"disambiguationData":[OSD([subQ6,subQ8,subQ9,subQ7,subQ4,subQ3,subQ2,subQ1,subQ0,subQ5,subQ10,subQ11])],"isStart":true})});}
            var sketch = newSketch(context, id + "F16", { "sketchPlane" : qUnion([Q0])});
            skLineSegment(sketch, "E79.0", {"start": v(-70, 90) * mm, "end": v(70, 90) * mm});
            skLineSegment(sketch, "E79.1", {"start": v(80, -80) * mm, "end": v(80, 80) * mm});
            skLineSegment(sketch, "E79.2", {"start": v(-70, -90) * mm, "end": v(70, -90) * mm});
            skLineSegment(sketch, "E79.3", {"start": v(-80, -80) * mm, "end": v(-80, 80) * mm});
            skArc(sketch, "E79.4", {"start": v(-80, -80) * mm, "mid": v(-77.07, -87.07) * mm, "end": v(-70, -90) * mm});
            skCircle(sketch, "E79.5", {"center": v(-60, -67.5) * mm, "radius": 4 * mm});
            skArc(sketch, "E79.6", {"start": v(-60, -40.3) * mm, "mid": v(-58.99, -44.68) * mm, "end": v(-56.15, -48.18) * mm});
            skArc(sketch, "E79.7", {"start": v(-56.15, -48.18) * mm, "mid": v(0, -67.5) * mm, "end": v(56.15, -48.18) * mm});
            skLineSegment(sketch, "E79.8", {"start": v(-60, 40.3) * mm, "end": v(-60, -40.3) * mm});
            skArc(sketch, "E79.9", {"start": v(70, -90) * mm, "mid": v(77.07, -87.07) * mm, "end": v(80, -80) * mm});
            skCircle(sketch, "E79.10", {"center": v(60, -67.5) * mm, "radius": 4 * mm});
            skArc(sketch, "E79.11", {"start": v(56.15, -48.18) * mm, "mid": v(58.99, -44.68) * mm, "end": v(60, -40.3) * mm});
            skLineSegment(sketch, "E79.12", {"start": v(60, 40.3) * mm, "end": v(60, -40.3) * mm});
            skArc(sketch, "E79.13", {"start": v(80, 80) * mm, "mid": v(77.07, 87.07) * mm, "end": v(70, 90) * mm});
            skArc(sketch, "E79.14", {"start": v(60, 40.3) * mm, "mid": v(58.99, 44.68) * mm, "end": v(56.15, 48.18) * mm});
            skCircle(sketch, "E79.15", {"center": v(60, 67.5) * mm, "radius": 4 * mm});
            skArc(sketch, "E79.16", {"start": v(56.15, 48.18) * mm, "mid": v(0, 67.5) * mm, "end": v(-56.15, 48.18) * mm});
            skArc(sketch, "E79.17", {"start": v(-56.15, 48.18) * mm, "mid": v(-58.99, 44.68) * mm, "end": v(-60, 40.3) * mm});
            skArc(sketch, "E79.18", {"start": v(-70, 90) * mm, "mid": v(-77.07, 87.07) * mm, "end": v(-80, 80) * mm});
            skCircle(sketch, "E79.19", {"center": v(-60, 67.5) * mm, "radius": 4 * mm});
            skCircle(sketch, "E80", {"center": v(0, 114.51) * mm, "radius": 6 * mm});
            skPoint(sketch, "E80.centerSnap0", {"position": v(0, 67.5) * mm});
            skLineSegment(sketch, "E81", {"start": v(-15, 108) * mm, "end": v(-33, 90) * mm});
            skLineSegment(sketch, "E82", {"start": v(15, 108) * mm, "end": v(33, 90) * mm});
            skLineSegment(sketch, "E83", {"start": v(-15, 108) * mm, "end": v(-15, 114.51) * mm});
            skLineSegment(sketch, "E84", {"start": v(15, 108) * mm, "end": v(15, 114.51) * mm});
            skArc(sketch, "E85", {"start": v(15, 114.51) * mm, "mid": v(0, 129.51) * mm, "end": v(-15, 114.51) * mm});
            skLineSegment(sketch, "E86", {"start": v(0, 0) * mm, "end": v(-80, 0) * mm, "construction": true});
            skLineSegment(sketch, "E87", {"start": v(0, 0) * mm, "end": v(80, 0) * mm, "construction": true});
            skLineSegment(sketch, "E88.MirrorCS", {"start": v(15, -108) * mm, "end": v(33, -90) * mm});
            skLineSegment(sketch, "E89.MirrorCS", {"start": v(-15, -108) * mm, "end": v(-33, -90) * mm});
            skLineSegment(sketch, "E90.MirrorCS", {"start": v(-15, -108) * mm, "end": v(-15, -114.51) * mm});
            skLineSegment(sketch, "E91.MirrorCS", {"start": v(15, -108) * mm, "end": v(15, -114.51) * mm});
            skArc(sketch, "E92.MirrorCS", {"start": v(15, -114.51) * mm, "mid": v(0, -129.51) * mm, "end": v(-15, -114.51) * mm});
            skCircle(sketch, "E93.MirrorC", {"center": v(0, -114.51) * mm, "radius": 6 * mm});
            skSolve(sketch);
        }
        {
            var Q0;
            Q0=makeQuery(id+"F16.imprint","IMPRINT",FACE,{"disambiguationData":[TD([[makeQuery(id+"F16.imprint","IMPRINT",EDGE,{"derivedFrom":sQuery(id+"F16.wireOp",EDGE,"E80")}),-1.0]])]});
            var Q1;
            Q1=makeQuery(id+"F16.imprint","IMPRINT",FACE,{"disambiguationData":[TD([[makeQuery(id+"F16.imprint","IMPRINT",EDGE,{"derivedFrom":sQuery(id+"F16.wireOp",EDGE,"E79.1")}),1.0]])]});
            var Q2;
            {var subQ1=sQuery(id+"F16.wireOp",EDGE,"E88.MirrorCS");Q2=makeQuery(id+"F16.imprint","IMPRINT",FACE,{"disambiguationData":[TD([[makeQuery(id+"F16.imprint","IMPRINT",EDGE,{"derivedFrom":subQ1}),1.0]])]});}
            var Q3;
            Q3=makeQuery(id+"F2.opExtrude","CAP_FACE",FACE,{"disambiguationData":[OSD([sQuery(id+"F0.wireOp",EDGE,"E12"),sQuery(id+"F0.wireOp",EDGE,"E13"),sQuery(id+"F0.wireOp",EDGE,"E14"),sQuery(id+"F0.wireOp",EDGE,"E15"),sQuery(id+"F0.wireOp",EDGE,"E17.filletArc"),sQuery(id+"F0.wireOp",EDGE,"E18.filletArc"),sQuery(id+"F0.wireOp",EDGE,"E19.filletArc"),sQuery(id+"F0.wireOp",EDGE,"E20.filletArc"),sQuery(id+"F0.wireOp",EDGE,"E25.0"),sQuery(id+"F0.wireOp",EDGE,"E25.1"),sQuery(id+"F0.wireOp",EDGE,"E25.2"),sQuery(id+"F0.wireOp",EDGE,"E25.3"),sQuery(id+"F0.wireOp",EDGE,"E25.4"),sQuery(id+"F0.wireOp",EDGE,"E25.5"),sQuery(id+"F0.wireOp",EDGE,"E25.6"),sQuery(id+"F0.wireOp",EDGE,"E25.7")])],"isStart":false});
            extrude(context, id + "F17", {"entities" : qUnion([Q0, Q1, Q2]), "endBound" : BoundingType.UP_TO_SURFACE, "endBoundEntityFace" : qUnion([Q3]), "depth" : 25 * mm});
        }
    });
